# Revit family: BE_50216.1_de_DE
name_source: partatom
category: Leuchten
revit_build: Autodesk Revit 2015 (Build: 20160512_0715(x64)
units: mm (PartAtom-declared; Revit-internal decimal feet)

## types (2) — shared parameters
AC/DC = AC/DC
Aktualisierung = 2017-09-29T04:10:01
BEGA_Dummy = Nein
BEGA_IES = Ja
BEGA_Intern = Ja
BEGA_Intern_Konstruktion = Ja
BEGA_Intern_an = Ja
BEGA_Intern_aus = Ja
Befestigungsabstand = 900 mm
Befestigungsbohrung = Ø 5,5 mm
Beschreibung = Decken- und Wandleuchte
Beschreibung_Sonderanfertigung = Hier können Sie Informationen zur Sonderanfertigung eintragen.
CE_Konformität = ja
Energieeffizienzklasse = LED A++ - A
Farbfilter = 16777215
Farbtemperaturverschiebung bei Dämpfen der Lampe = <Keine Auswahl>
Farbwiedergabeindex = Ra > 90
Frequenz = 0/50-60 Hz
Gewicht = 2.7 kg
Hersteller = BEGA
Lampe = LED 35.2 W
Lastklassifizierung = Beleuchtung
Lebensdauerkriterien = L70B50 @ 25 °C = 331000 h
Logo = BEGA_Logo.png
M_A = Nein
M_G = Nein
M_W = Nein
Material_02 = BEGA_Oberfläche_Silber_matt
Material_03 = BEGA_Oberfläche_Weiss_matt
Material_05 = BEGA_Oberfläche_Aluminium Guss
Material_06 = BEGA_Oberfläche_Edelstahl_gebürstet
Material_09 = BEGA_Glas_klar
Material_11 = BEGA_Glas_opal
Material_14 = BEGA_Kunststoff_opal
Material_15 = BEGA_Leuchtmedium_matt
Material_17 = BEGA_Reflektor
Neigungswinkel = 0.00°
Produktdatenblatt = http://www.bega.de
Scheinlast = 0 VA
Schutzklasse = I
Sonderanfertigung = Nein
Spannung = 240 V
URL = http://www.bega.de
Umgebungstemperatur = 25 °C
zero-valued in all types: Vorgabe-Ansicht

## per-type parameters (varying)
| type | Bestellnummer | Datei für fotometrisches Netz | Farbtemperatur | LED_Modulbezeichnung | Lampenlichtstrom | Leuchtenlichtstrom | Modell |
| BEGA_50216.1_K4 | 50216.1K4 | BE_50216K4.IES | 4000 K | 4x LED-0694/940 | 6200 lm | 5327 lm | 50216.1K4 |
| BEGA_50216.1_K3 | 50216.1 | BE_50216.IES | 3000 K | 4x LED-0694/930 | 5900 lm | 5070 lm | 50216.1 |
